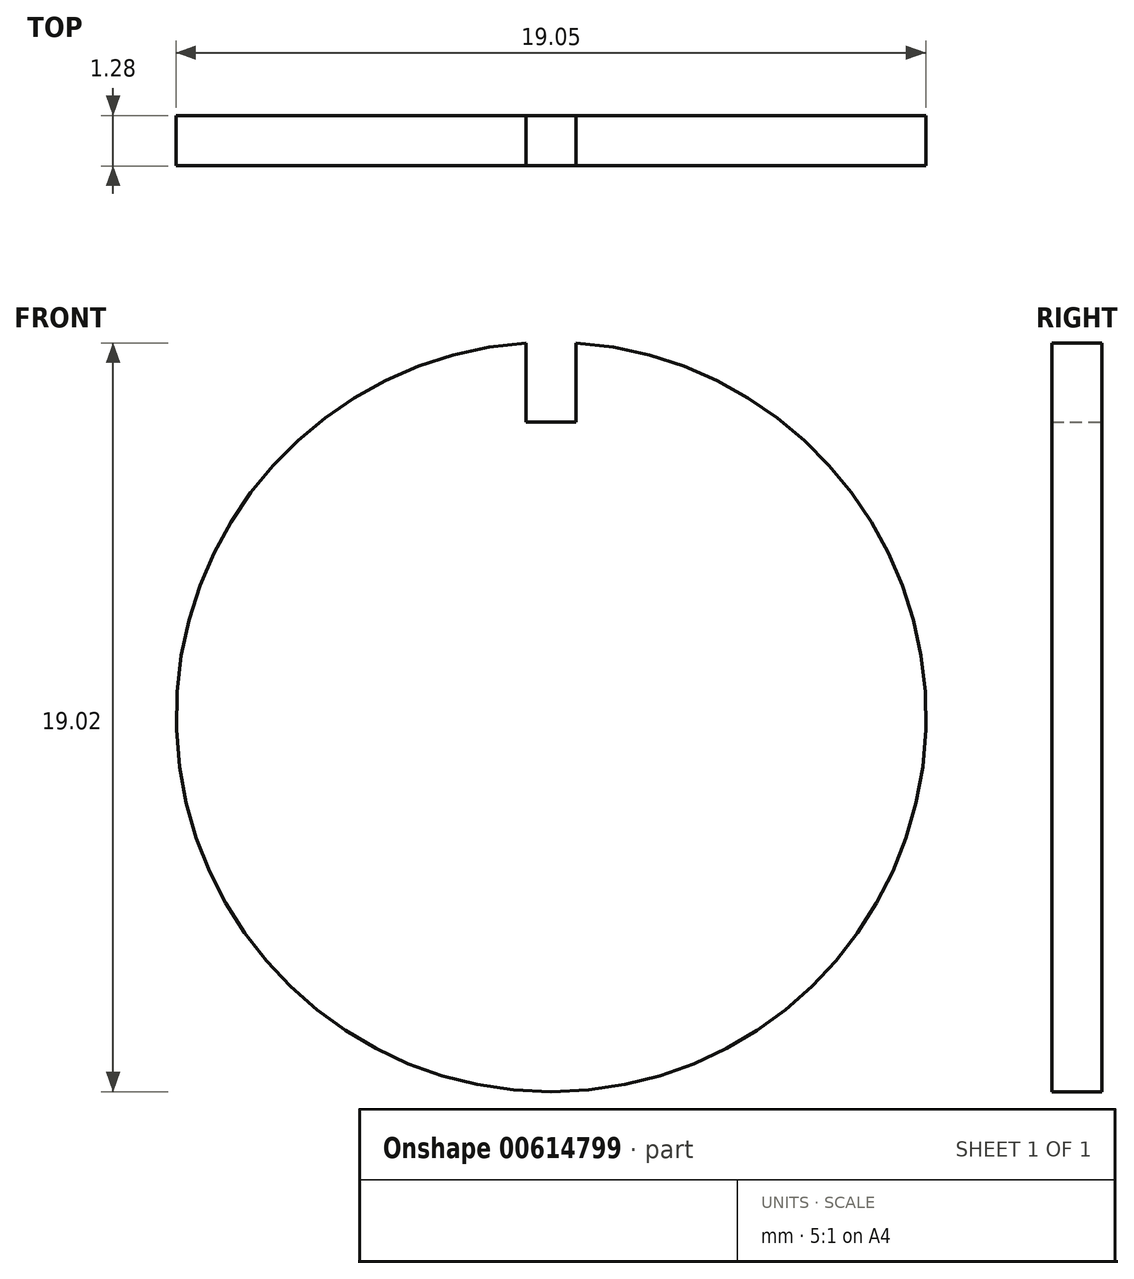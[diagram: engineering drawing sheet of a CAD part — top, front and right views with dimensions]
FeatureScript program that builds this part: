
annotation { "Feature Type Name" : "Feature", "Feature Type Description" : "" }
export const myFeature = defineFeature(function(context is Context, id is Id, definition is map)
    precondition{}
    {
        {
            var Q0;
            Q0=qCreatedBy(makeId("Front.planeOp"),FACE);
            var sketch = newSketch(context, id + "F0", { "sketchPlane" : qUnion([Q0])});
            skArc(sketch, "E0", {"start": v(-0.64, 9.5) * mm, "mid": v(0, -9.53) * mm, "end": v(0.63, 9.5) * mm});
            skLineSegment(sketch, "E1.bottom", {"start": v(0.63, 7.5) * mm, "end": v(-0.64, 7.5) * mm});
            skLineSegment(sketch, "E1.left", {"start": v(0.63, 7.5) * mm, "end": v(0.63, 9.5) * mm});
            skLineSegment(sketch, "E1.right", {"start": v(-0.64, 7.5) * mm, "end": v(-0.64, 9.5) * mm});
            skSolve(sketch);
        }
        {
            var Q0;
            Q0=makeQuery(id+"F0.imprint","IMPRINT",FACE,{"disambiguationData":[TD([[makeQuery(id+"F0.imprint","IMPRINT",EDGE,{"derivedFrom":sQuery(id+"F0.wireOp",EDGE,"E0")}),1.0]])]});
            extrude(context, id + "F1", {"entities" : qUnion([Q0]), "endBound" : BoundingType.SYMMETRIC, "depth" : 1.27 * mm, "offsetDistance" : 25.4 * mm});
        }
    });
